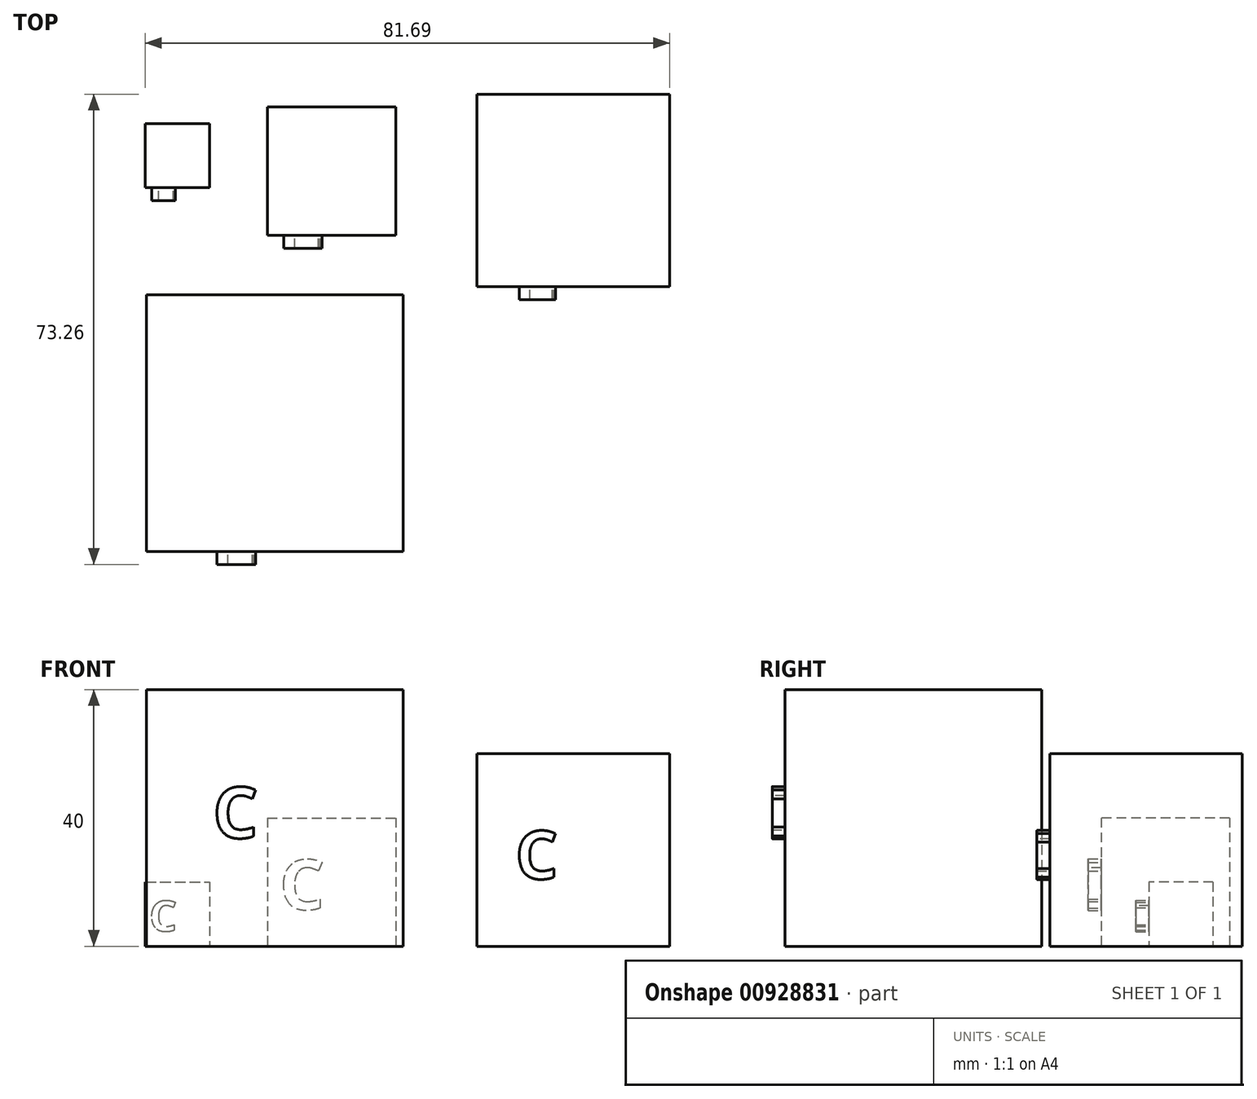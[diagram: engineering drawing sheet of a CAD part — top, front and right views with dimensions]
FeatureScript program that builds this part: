
annotation { "Feature Type Name" : "Feature", "Feature Type Description" : "" }
export const myFeature = defineFeature(function(context is Context, id is Id, definition is map)
    precondition{}
    {
        {
            var Q0;
            Q0=qCreatedBy(makeId("Top.planeOp"),FACE);
            var sketch = newSketch(context, id + "F0", { "sketchPlane" : qUnion([Q0])});
            skLineSegment(sketch, "E0.bottom", {"start": v(-41.19, 33.52) * mm, "end": v(-31.19, 33.52) * mm});
            skLineSegment(sketch, "E0.top", {"start": v(-41.19, 23.52) * mm, "end": v(-31.19, 23.52) * mm});
            skLineSegment(sketch, "E0.left", {"start": v(-41.19, 33.52) * mm, "end": v(-41.19, 23.52) * mm});
            skLineSegment(sketch, "E0.right", {"start": v(-31.19, 33.52) * mm, "end": v(-31.19, 23.52) * mm});
            skSolve(sketch);
        }
        {
            var Q0;
            Q0 = qSketchRegion(id + "F0", true);
            extrude(context, id + "F1", {"entities" : qUnion([Q0]), "depth" : 10 * mm, "offsetDistance" : 25 * mm});
        }
        {
            var Q0;
            Q0=qCreatedBy(makeId("Top.planeOp"),FACE);
            var sketch = newSketch(context, id + "F2", { "sketchPlane" : qUnion([Q0])});
            skLineSegment(sketch, "E1.bottom", {"start": v(-22.12, 36.08) * mm, "end": v(-2.12, 36.08) * mm});
            skLineSegment(sketch, "E1.top", {"start": v(-22.12, 16.08) * mm, "end": v(-2.12, 16.08) * mm});
            skLineSegment(sketch, "E1.left", {"start": v(-22.12, 36.08) * mm, "end": v(-22.12, 16.08) * mm});
            skLineSegment(sketch, "E1.right", {"start": v(-2.12, 36.08) * mm, "end": v(-2.12, 16.08) * mm});
            skSolve(sketch);
        }
        {
            var Q0;
            Q0 = qSketchRegion(id + "F2", true);
            extrude(context, id + "F3", {"entities" : qUnion([Q0]), "depth" : 20 * mm, "offsetDistance" : 25 * mm});
        }
        {
            var Q0;
            Q0=qCreatedBy(makeId("Top.planeOp"),FACE);
            var sketch = newSketch(context, id + "F4", { "sketchPlane" : qUnion([Q0])});
            skLineSegment(sketch, "E2.bottom", {"start": v(10.5, 38.08) * mm, "end": v(40.5, 38.08) * mm});
            skLineSegment(sketch, "E2.top", {"start": v(10.5, 8.08) * mm, "end": v(40.5, 8.08) * mm});
            skLineSegment(sketch, "E2.left", {"start": v(10.5, 38.08) * mm, "end": v(10.5, 8.08) * mm});
            skLineSegment(sketch, "E2.right", {"start": v(40.5, 38.08) * mm, "end": v(40.5, 8.08) * mm});
            skSolve(sketch);
        }
        {
            var Q0;
            Q0 = qSketchRegion(id + "F4", true);
            extrude(context, id + "F5", {"entities" : qUnion([Q0]), "depth" : 30 * mm, "offsetDistance" : 25 * mm});
        }
        {
            var Q0;
            Q0=qCreatedBy(makeId("Top.planeOp"),FACE);
            var sketch = newSketch(context, id + "F6", { "sketchPlane" : qUnion([Q0])});
            skLineSegment(sketch, "E3.bottom", {"start": v(-41.01, 6.82) * mm, "end": v(-1.01, 6.82) * mm});
            skLineSegment(sketch, "E3.top", {"start": v(-41.01, -33.18) * mm, "end": v(-1.01, -33.18) * mm});
            skLineSegment(sketch, "E3.left", {"start": v(-41.01, 6.82) * mm, "end": v(-41.01, -33.18) * mm});
            skLineSegment(sketch, "E3.right", {"start": v(-1.01, 6.82) * mm, "end": v(-1.01, -33.18) * mm});
            skSolve(sketch);
        }
        {
            var Q0;
            Q0=makeQuery(id+"F6.imprint","IMPRINT",FACE,{"disambiguationData":[TD([[makeQuery(id+"F6.imprint","IMPRINT",EDGE,{"derivedFrom":sQuery(id+"F6.wireOp",EDGE,"E3.bottom")}),-1.0]])]});
            extrude(context, id + "F7", {"entities" : qUnion([Q0]), "depth" : 40 * mm, "offsetDistance" : 25 * mm});
        }
        {
            var Q0;
            Q0=makeQuery(id+"F1.opExtrude","SWEPT_FACE",FACE,{"disambiguationData":[OSD([sQuery(id+"F0.wireOp",EDGE,"E0.top")])]});
            var sketch = newSketch(context, id + "F8", { "sketchPlane" : qUnion([Q0])});
            skText(sketch, "E4", { "text": "C", "fontName": "OpenSans-Bold.ttf"});
            const initialGuessF8  = {"E4": [-0.04056, 0.00231, 1, 0, 0.00484]};
            skSetInitialGuess(sketch, initialGuessF8);
            skSolve(sketch);
        }
        {
            var Q0;
            Q0 = qSketchRegion(id + "F8", true);
            extrude(context, id + "F9", {"entities" : qUnion([Q0]), "operationType" : NewBodyOperationType.ADD, "depth" : 2 * mm, "offsetDistance" : 25 * mm});
        }
        {
            var Q0;
            Q0=makeQuery(id+"F3.opExtrude","SWEPT_FACE",FACE,{"disambiguationData":[OSD([sQuery(id+"F2.wireOp",EDGE,"E1.top")])]});
            var sketch = newSketch(context, id + "F10", { "sketchPlane" : qUnion([Q0])});
            skText(sketch, "E5", { "text": "C", "fontName": "OpenSans-Bold.ttf"});
            const initialGuessF10  = {"E5": [-0.02026, 0.00568, 1, 0, 0.0079]};
            skSetInitialGuess(sketch, initialGuessF10);
            skSolve(sketch);
        }
        {
            var Q0;
            Q0 = qSketchRegion(id + "F10", true);
            extrude(context, id + "F11", {"entities" : qUnion([Q0]), "operationType" : NewBodyOperationType.ADD, "depth" : 2 * mm, "offsetDistance" : 25 * mm});
        }
        {
            var Q0;
            Q0=makeQuery(id+"F5.opExtrude","SWEPT_FACE",FACE,{"disambiguationData":[OSD([sQuery(id+"F4.wireOp",EDGE,"E2.top")])]});
            var sketch = newSketch(context, id + "F12", { "sketchPlane" : qUnion([Q0])});
            skText(sketch, "E6", { "text": "C", "fontName": "OpenSans-Bold.ttf"});
            const initialGuessF12  = {"E6": [0.01648, 0.0105, 1, 0, 0.00752]};
            skSetInitialGuess(sketch, initialGuessF12);
            skSolve(sketch);
        }
        {
            var Q0;
            Q0 = qSketchRegion(id + "F12", true);
            extrude(context, id + "F13", {"entities" : qUnion([Q0]), "operationType" : NewBodyOperationType.ADD, "depth" : 2 * mm, "offsetDistance" : 25 * mm});
        }
        {
            var Q0;
            Q0=makeQuery(id+"F7.opExtrude","SWEPT_FACE",FACE,{"disambiguationData":[OSD([sQuery(id+"F6.wireOp",EDGE,"E3.top")])]});
            var sketch = newSketch(context, id + "F14", { "sketchPlane" : qUnion([Q0])});
            skText(sketch, "E7", { "text": "C", "fontName": "OpenSans-Bold.ttf"});
            const initialGuessF14  = {"E7": [-0.03066, 0.01687, 1, 0, 0.00798]};
            skSetInitialGuess(sketch, initialGuessF14);
            skSolve(sketch);
        }
        {
            var Q0;
            Q0 = qSketchRegion(id + "F14", true);
            extrude(context, id + "F15", {"entities" : qUnion([Q0]), "operationType" : NewBodyOperationType.ADD, "depth" : 2 * mm, "offsetDistance" : 25 * mm});
        }
    });
